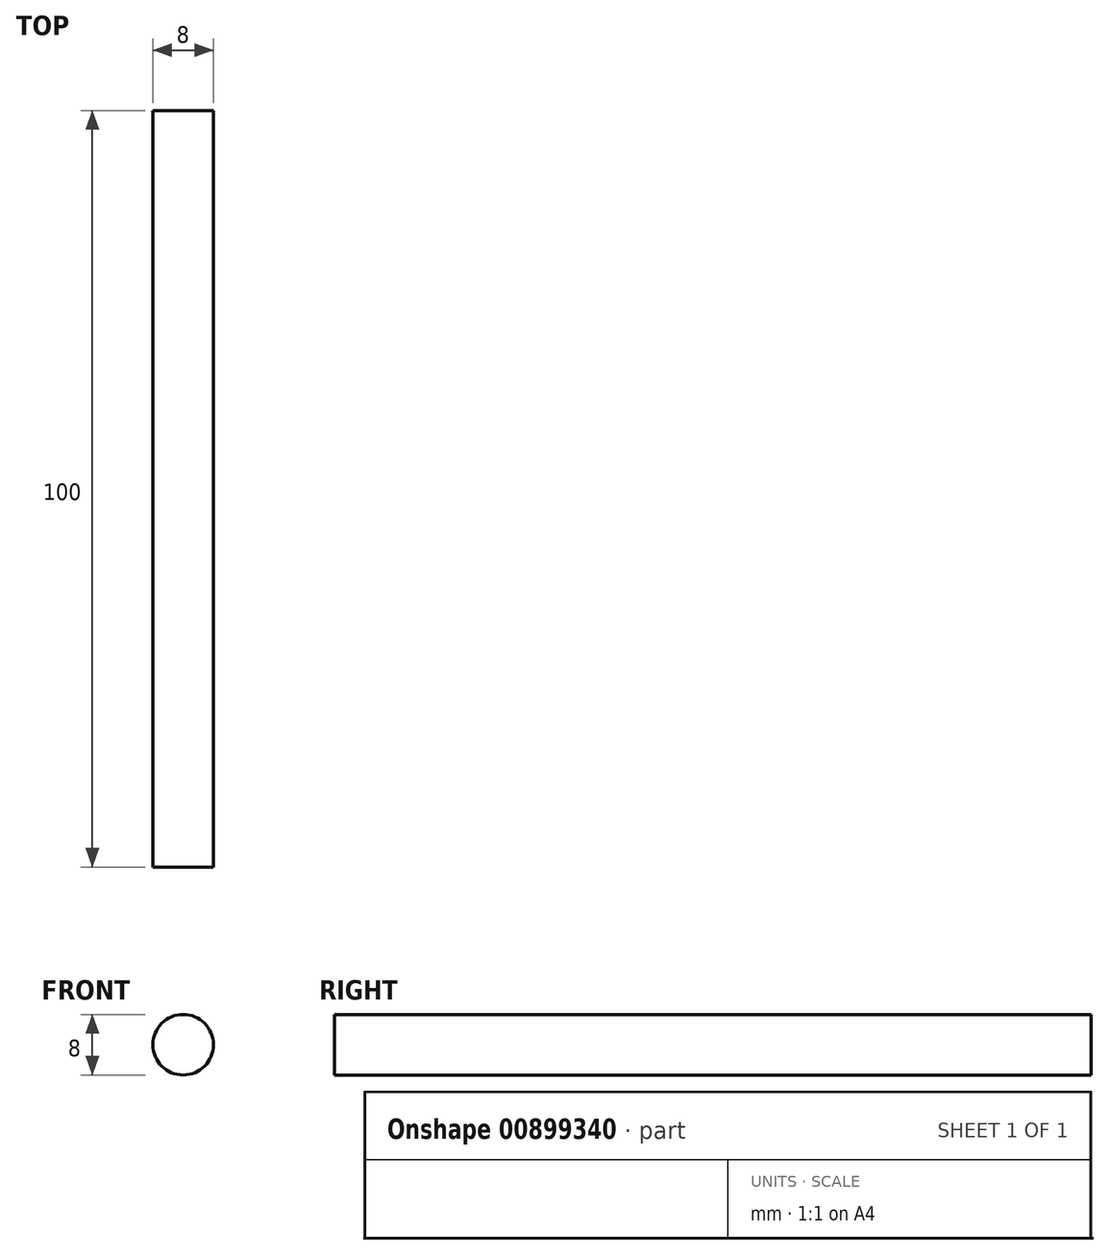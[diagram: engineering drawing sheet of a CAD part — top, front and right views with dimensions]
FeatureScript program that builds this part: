
annotation { "Feature Type Name" : "Feature", "Feature Type Description" : "" }
export const myFeature = defineFeature(function(context is Context, id is Id, definition is map)
    precondition{}
    {
        {
            var Q0;
            Q0=qCreatedBy(makeId("Front.planeOp"),FACE);
            var sketch = newSketch(context, id + "F0", { "sketchPlane" : qUnion([Q0])});
            skCircle(sketch, "E0", {"center": v(0, 0) * mm, "radius": 4 * mm});
            skSolve(sketch);
        }
        {
            var Q0;
            Q0=makeQuery(id+"F0.imprint","IMPRINT",FACE,{"disambiguationData":[TD([[makeQuery(id+"F0.imprint","IMPRINT",EDGE,{"derivedFrom":sQuery(id+"F0.wireOp",EDGE,"E0")}),1.0]])]});
            extrude(context, id + "F1", {"entities" : qUnion([Q0]), "oppositeDirection" : true, "depth" : 100 * mm, "offsetDistance" : 25 * mm});
        }
    });
